# Revit family: KIT_HYBRID
name_source: partatom
category: Attrezzatura meccanica
units: mm (PartAtom-declared; Revit-internal decimal feet)

## family parameters
Basato su piano di lavoro = No
Classificazione = Nessuno
Condiviso = No
Mantieni orientamento annotazione = No
Punto di calcolo locali = No
Quota connettore circolare = Usa diametro
Sempre verticale = Sì
Taglio con vuoti quando caricato = No
Tipo di parte = Normale

## types (1)
- Kit Hybrid
    Date of publishing = 04/10/2023
    Depth = 240 mm  [stored 0.787402 ft]
    Height = 410 mm  [stored 1.34514 ft]
    Hydronic Return Diameter = 26 mm
    Hydronic Supply Diameter = 26 mm
    Manufacturer country = Italy
    Manufacturer name = Italtherm S.p.A.
    Material main = Metal
    Material secondary = Plastic
    Max.operating ambient temperature = 50 °C
    Maximum system pressure = 1 Bar
    Min.operating ambient temperature = -10 °C
    Power supply | Frequency (Hz) = 50 Hz
    Power supply | Phase = 1
    Power supply | Voltage (V) = 230 V
    Product family = Heating
    Product group = Thermal unit
    Prospetto di default = 0 mm  [stored 0 ft]
    Refrigerant Gas = 16 mm  [stored 0.0524934 ft]
    Sound power = 54 dB
    Weight = 16,20 kg
    Width = 440 mm  [stored 1.44357 ft]

note: [stored X ft] marks values corroborated as IEEE doubles in the binary element streams (Revit-internal decimal feet)
